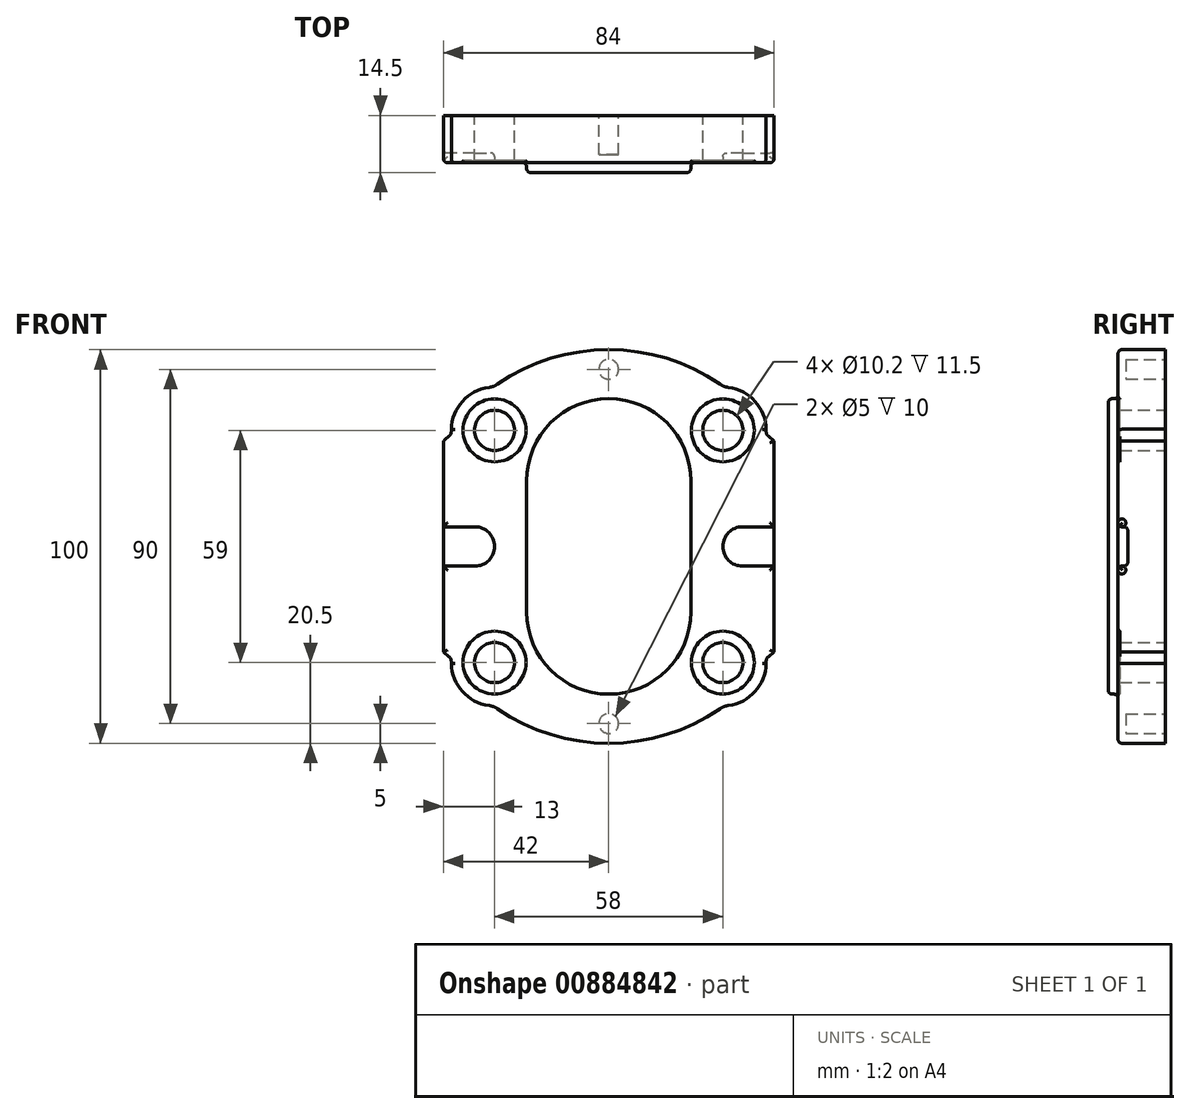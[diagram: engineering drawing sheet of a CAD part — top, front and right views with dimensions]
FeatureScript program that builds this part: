
annotation { "Feature Type Name" : "Feature", "Feature Type Description" : "" }
export const myFeature = defineFeature(function(context is Context, id is Id, definition is map)
    precondition{}
    {
        {
            var Q0;
            Q0=qCreatedBy(makeId("Front.planeOp"),FACE);
            var sketch = newSketch(context, id + "F0", { "sketchPlane" : qUnion([Q0])});
            skArc(sketch, "E0", {"start": v(-28.27, 41.24) * mm, "mid": v(0, 50) * mm, "end": v(28.27, 41.24) * mm});
            skCircle(sketch, "E1", {"center": v(-29, 29.5) * mm, "radius": 5.1 * mm});
            skCircle(sketch, "E2", {"center": v(29, 29.5) * mm, "radius": 5.1 * mm});
            skArc(sketch, "E3", {"start": v(-30.45, 40.4) * mm, "mid": v(-37.18, 36.85) * mm, "end": v(-40, 29.77) * mm});
            skLineSegment(sketch, "E4", {"start": v(-40, 29.77) * mm, "end": v(-40, 29.18) * mm});
            skPoint(sketch, "E5.visualSharp", {"position": v(-29.33, 40.5) * mm});
            skArc(sketch, "E5.filletArc", {"start": v(-30.45, 40.4) * mm, "mid": v(-29.31, 40.7) * mm, "end": v(-28.27, 41.24) * mm});
            skArc(sketch, "E6.MirrorCS", {"start": v(30.45, 40.4) * mm, "mid": v(37.18, 36.85) * mm, "end": v(40, 29.77) * mm});
            skLineSegment(sketch, "E7.MirrorCS", {"start": v(40, 29.77) * mm, "end": v(40, 29.18) * mm});
            skPoint(sketch, "E8.newPointA", {"position": v(29.33, 40.5) * mm});
            skPoint(sketch, "E8.newPointB", {"position": v(30.45, 40.4) * mm});
            skArc(sketch, "E8.filletArc", {"start": v(28.27, 41.24) * mm, "mid": v(29.31, 40.7) * mm, "end": v(30.45, 40.4) * mm});
            skLineSegment(sketch, "E9", {"start": v(-40.55, 28.02) * mm, "end": v(-42, 26.83) * mm});
            skLineSegment(sketch, "E10", {"start": v(-42, 26.83) * mm, "end": v(-42, 0) * mm});
            skPoint(sketch, "E11.visualSharp", {"position": v(-40, 28.47) * mm});
            skArc(sketch, "E11.filletArc", {"start": v(-40.55, 28.02) * mm, "mid": v(-40.14, 28.54) * mm, "end": v(-40, 29.18) * mm});
            skLineSegment(sketch, "E12.MirrorCS", {"start": v(42, 26.83) * mm, "end": v(42, 0) * mm});
            skArc(sketch, "E13.MirrorCS", {"start": v(40.55, 28.02) * mm, "mid": v(40.14, 28.54) * mm, "end": v(40, 29.18) * mm});
            skLineSegment(sketch, "E14.MirrorCS", {"start": v(40.55, 28.02) * mm, "end": v(42, 26.83) * mm});
            skPoint(sketch, "E15.orphan", {"position": v(40, 28.47) * mm});
            skLineSegment(sketch, "E16.MirrorCS", {"start": v(40, -29.77) * mm, "end": v(40, -29.18) * mm});
            skArc(sketch, "E17.MirrorCS", {"start": v(40.55, -28.02) * mm, "mid": v(40.14, -28.54) * mm, "end": v(40, -29.18) * mm});
            skArc(sketch, "E18.MirrorCS", {"start": v(-40.55, -28.02) * mm, "mid": v(-40.14, -28.54) * mm, "end": v(-40, -29.18) * mm});
            skLineSegment(sketch, "E19.MirrorCS", {"start": v(-40, -29.77) * mm, "end": v(-40, -29.18) * mm});
            skArc(sketch, "E20.MirrorCS", {"start": v(28.27, -41.24) * mm, "mid": v(29.31, -40.7) * mm, "end": v(30.45, -40.4) * mm});
            skArc(sketch, "E21.MirrorCS", {"start": v(-30.45, -40.4) * mm, "mid": v(-29.31, -40.7) * mm, "end": v(-28.27, -41.24) * mm});
            skLineSegment(sketch, "E22.MirrorCS", {"start": v(40.55, -28.02) * mm, "end": v(42, -26.83) * mm});
            skLineSegment(sketch, "E23.MirrorCS", {"start": v(-40.55, -28.02) * mm, "end": v(-42, -26.83) * mm});
            skCircle(sketch, "E24.MirrorC", {"center": v(-29, -29.5) * mm, "radius": 5.1 * mm});
            skPoint(sketch, "E25.MirrorP", {"position": v(40, -28.47) * mm});
            skPoint(sketch, "E26.MirrorP", {"position": v(30.45, -40.4) * mm});
            skLineSegment(sketch, "E27.MirrorCS", {"start": v(-42, -26.83) * mm, "end": v(-42, 0) * mm});
            skPoint(sketch, "E28.MirrorP", {"position": v(29.33, -40.5) * mm});
            skCircle(sketch, "E29.MirrorC", {"center": v(29, -29.5) * mm, "radius": 5.1 * mm});
            skArc(sketch, "E30.MirrorCS", {"start": v(30.45, -40.4) * mm, "mid": v(37.18, -36.85) * mm, "end": v(40, -29.77) * mm});
            skArc(sketch, "E31.MirrorCS", {"start": v(-28.27, -41.24) * mm, "mid": v(0, -50) * mm, "end": v(28.27, -41.24) * mm});
            skPoint(sketch, "E32.MirrorP", {"position": v(-29.33, -40.5) * mm});
            skLineSegment(sketch, "E33.MirrorCS", {"start": v(42, -26.83) * mm, "end": v(42, 0) * mm});
            skArc(sketch, "E34.MirrorCS", {"start": v(-30.45, -40.4) * mm, "mid": v(-37.18, -36.85) * mm, "end": v(-40, -29.77) * mm});
            skPoint(sketch, "E35.MirrorP", {"position": v(-40, -28.47) * mm});
            skSolve(sketch);
        }
        {
            var Q0;
            Q0 = qSketchRegion(id + "F0", true);
            extrude(context, id + "F1", {"entities" : qUnion([Q0]), "depth" : 12 * mm, "offsetDistance" : 25 * mm});
        }
        {
            var Q0;
            Q0=makeQuery(id+"F1.opExtrude","CAP_FACE",FACE,{"disambiguationData":[OSD([sQuery(id+"F0.wireOp",EDGE,"E0"),sQuery(id+"F0.wireOp",EDGE,"E1"),sQuery(id+"F0.wireOp",EDGE,"E2"),sQuery(id+"F0.wireOp",EDGE,"E3"),sQuery(id+"F0.wireOp",EDGE,"E4"),sQuery(id+"F0.wireOp",EDGE,"E5.filletArc"),sQuery(id+"F0.wireOp",EDGE,"E6.MirrorCS"),sQuery(id+"F0.wireOp",EDGE,"E8.filletArc"),sQuery(id+"F0.wireOp",EDGE,"E9"),sQuery(id+"F0.wireOp",EDGE,"E10"),sQuery(id+"F0.wireOp",EDGE,"E11.filletArc"),sQuery(id+"F0.wireOp",EDGE,"E12.MirrorCS"),sQuery(id+"F0.wireOp",EDGE,"E7.MirrorCS"),sQuery(id+"F0.wireOp",EDGE,"E13.MirrorCS"),sQuery(id+"F0.wireOp",EDGE,"E14.MirrorCS"),sQuery(id+"F0.wireOp",EDGE,"E17.MirrorCS"),sQuery(id+"F0.wireOp",EDGE,"E16.MirrorCS"),sQuery(id+"F0.wireOp",EDGE,"E18.MirrorCS"),sQuery(id+"F0.wireOp",EDGE,"E19.MirrorCS"),sQuery(id+"F0.wireOp",EDGE,"E20.MirrorCS"),sQuery(id+"F0.wireOp",EDGE,"E21.MirrorCS"),sQuery(id+"F0.wireOp",EDGE,"E22.MirrorCS"),sQuery(id+"F0.wireOp",EDGE,"E23.MirrorCS"),sQuery(id+"F0.wireOp",EDGE,"E24.MirrorC"),sQuery(id+"F0.wireOp",EDGE,"E27.MirrorCS"),sQuery(id+"F0.wireOp",EDGE,"E29.MirrorC"),sQuery(id+"F0.wireOp",EDGE,"E30.MirrorCS"),sQuery(id+"F0.wireOp",EDGE,"E31.MirrorCS"),sQuery(id+"F0.wireOp",EDGE,"E33.MirrorCS"),sQuery(id+"F0.wireOp",EDGE,"E34.MirrorCS")])],"isStart":false});
            var sketch = newSketch(context, id + "F2", { "sketchPlane" : qUnion([Q0])});
            skLineSegment(sketch, "E36", {"start": v(0, 33.36) * mm, "end": v(0, 0) * mm, "construction": true});
            skLineSegment(sketch, "E37", {"start": v(0, 0) * mm, "end": v(54.4, 0) * mm, "construction": true});
            skArc(sketch, "E38", {"start": v(20.85, 16.68) * mm, "mid": v(0, 37.53) * mm, "end": v(-20.85, 16.68) * mm});
            skArc(sketch, "E39.MirrorC", {"start": v(20.85, -16.68) * mm, "mid": v(0, -37.53) * mm, "end": v(-20.85, -16.68) * mm});
            skLineSegment(sketch, "E40", {"start": v(-20.85, 16.68) * mm, "end": v(-20.85, -16.68) * mm});
            skLineSegment(sketch, "E41", {"start": v(20.85, 16.68) * mm, "end": v(20.85, -16.68) * mm});
            skSolve(sketch);
        }
        {
            var Q0;
            Q0 = qSketchRegion(id + "F2", true);
            extrude(context, id + "F3", {"entities" : qUnion([Q0]), "operationType" : NewBodyOperationType.ADD, "depth" : 2.5 * mm, "offsetDistance" : 25 * mm});
        }
        {
            var Q0;
            Q0=makeQuery(id+"F1.opExtrude","CAP_FACE",FACE,{"disambiguationData":[OSD([sQuery(id+"F0.wireOp",EDGE,"E0"),sQuery(id+"F0.wireOp",EDGE,"E1"),sQuery(id+"F0.wireOp",EDGE,"E2"),sQuery(id+"F0.wireOp",EDGE,"E3"),sQuery(id+"F0.wireOp",EDGE,"E4"),sQuery(id+"F0.wireOp",EDGE,"E5.filletArc"),sQuery(id+"F0.wireOp",EDGE,"E6.MirrorCS"),sQuery(id+"F0.wireOp",EDGE,"E8.filletArc"),sQuery(id+"F0.wireOp",EDGE,"E9"),sQuery(id+"F0.wireOp",EDGE,"E10"),sQuery(id+"F0.wireOp",EDGE,"E11.filletArc"),sQuery(id+"F0.wireOp",EDGE,"E12.MirrorCS"),sQuery(id+"F0.wireOp",EDGE,"E7.MirrorCS"),sQuery(id+"F0.wireOp",EDGE,"E13.MirrorCS"),sQuery(id+"F0.wireOp",EDGE,"E14.MirrorCS"),sQuery(id+"F0.wireOp",EDGE,"E17.MirrorCS"),sQuery(id+"F0.wireOp",EDGE,"E16.MirrorCS"),sQuery(id+"F0.wireOp",EDGE,"E18.MirrorCS"),sQuery(id+"F0.wireOp",EDGE,"E19.MirrorCS"),sQuery(id+"F0.wireOp",EDGE,"E20.MirrorCS"),sQuery(id+"F0.wireOp",EDGE,"E21.MirrorCS"),sQuery(id+"F0.wireOp",EDGE,"E22.MirrorCS"),sQuery(id+"F0.wireOp",EDGE,"E23.MirrorCS"),sQuery(id+"F0.wireOp",EDGE,"E24.MirrorC"),sQuery(id+"F0.wireOp",EDGE,"E27.MirrorCS"),sQuery(id+"F0.wireOp",EDGE,"E29.MirrorC"),sQuery(id+"F0.wireOp",EDGE,"E30.MirrorCS"),sQuery(id+"F0.wireOp",EDGE,"E31.MirrorCS"),sQuery(id+"F0.wireOp",EDGE,"E33.MirrorCS"),sQuery(id+"F0.wireOp",EDGE,"E34.MirrorCS")])],"isStart":false});
            var sketch = newSketch(context, id + "F4", { "sketchPlane" : qUnion([Q0])});
            skArc(sketch, "E42", {"start": v(-34, -5) * mm, "mid": v(-29, 0) * mm, "end": v(-34, 5) * mm});
            skLineSegment(sketch, "E43.bottom", {"start": v(-34, 5) * mm, "end": v(-47.92, 5) * mm});
            skLineSegment(sketch, "E43.top", {"start": v(-34, -5) * mm, "end": v(-47.92, -5) * mm});
            skLineSegment(sketch, "E43.right", {"start": v(-47.92, 5) * mm, "end": v(-47.92, -5) * mm});
            skLineSegment(sketch, "E44.MirrorCS", {"start": v(34, -5) * mm, "end": v(47.92, -5) * mm});
            skLineSegment(sketch, "E45.MirrorCS", {"start": v(34, 5) * mm, "end": v(47.92, 5) * mm});
            skLineSegment(sketch, "E46.MirrorCS", {"start": v(47.92, 5) * mm, "end": v(47.92, -5) * mm});
            skArc(sketch, "E47.MirrorCS", {"start": v(34, -5) * mm, "mid": v(29, 0) * mm, "end": v(34, 5) * mm});
            skSolve(sketch);
        }
        {
            var Q0;
            Q0 = qSketchRegion(id + "F4", true);
            extrude(context, id + "F5", {"entities" : qUnion([Q0]), "operationType" : NewBodyOperationType.REMOVE, "oppositeDirection" : true, "depth" : 2.5 * mm, "offsetDistance" : 25 * mm});
        }
        {
            var Q0;
            Q0=makeQuery(id+"F1.opExtrude","CAP_FACE",FACE,{"disambiguationData":[OSD([sQuery(id+"F0.wireOp",EDGE,"E0"),sQuery(id+"F0.wireOp",EDGE,"E1"),sQuery(id+"F0.wireOp",EDGE,"E2"),sQuery(id+"F0.wireOp",EDGE,"E3"),sQuery(id+"F0.wireOp",EDGE,"E4"),sQuery(id+"F0.wireOp",EDGE,"E5.filletArc"),sQuery(id+"F0.wireOp",EDGE,"E6.MirrorCS"),sQuery(id+"F0.wireOp",EDGE,"E8.filletArc"),sQuery(id+"F0.wireOp",EDGE,"E9"),sQuery(id+"F0.wireOp",EDGE,"E10"),sQuery(id+"F0.wireOp",EDGE,"E11.filletArc"),sQuery(id+"F0.wireOp",EDGE,"E12.MirrorCS"),sQuery(id+"F0.wireOp",EDGE,"E7.MirrorCS"),sQuery(id+"F0.wireOp",EDGE,"E13.MirrorCS"),sQuery(id+"F0.wireOp",EDGE,"E14.MirrorCS"),sQuery(id+"F0.wireOp",EDGE,"E17.MirrorCS"),sQuery(id+"F0.wireOp",EDGE,"E16.MirrorCS"),sQuery(id+"F0.wireOp",EDGE,"E18.MirrorCS"),sQuery(id+"F0.wireOp",EDGE,"E19.MirrorCS"),sQuery(id+"F0.wireOp",EDGE,"E20.MirrorCS"),sQuery(id+"F0.wireOp",EDGE,"E21.MirrorCS"),sQuery(id+"F0.wireOp",EDGE,"E22.MirrorCS"),sQuery(id+"F0.wireOp",EDGE,"E23.MirrorCS"),sQuery(id+"F0.wireOp",EDGE,"E24.MirrorC"),sQuery(id+"F0.wireOp",EDGE,"E27.MirrorCS"),sQuery(id+"F0.wireOp",EDGE,"E29.MirrorC"),sQuery(id+"F0.wireOp",EDGE,"E30.MirrorCS"),sQuery(id+"F0.wireOp",EDGE,"E31.MirrorCS"),sQuery(id+"F0.wireOp",EDGE,"E33.MirrorCS"),sQuery(id+"F0.wireOp",EDGE,"E34.MirrorCS")])],"isStart":false});
            var sketch = newSketch(context, id + "F6", { "sketchPlane" : qUnion([Q0])});
            skCircle(sketch, "E48", {"center": v(-29, 29.5) * mm, "radius": 8 * mm});
            skCircle(sketch, "E49", {"center": v(29, 29.5) * mm, "radius": 8 * mm});
            skCircle(sketch, "E50", {"center": v(29, -29.5) * mm, "radius": 8 * mm});
            skCircle(sketch, "E51", {"center": v(-29, -29.5) * mm, "radius": 8 * mm});
            skSolve(sketch);
        }
        {
            var Q0;
            Q0 = qSketchRegion(id + "F6", true);
            extrude(context, id + "F7", {"entities" : qUnion([Q0]), "operationType" : NewBodyOperationType.REMOVE, "oppositeDirection" : true, "depth" : .5 * mm, "offsetDistance" : 25 * mm});
        }
        {
            var Q0;
            Q0=makeQuery(id+"F1.opExtrude","CAP_EDGE",EDGE,{"disambiguationData":[OSD([sQuery(id+"F0.wireOp",EDGE,"E0")])],"isStart":false});
            var Q1;
            {var subQ0=sQuery(id+"F0.wireOp",EDGE,"E33.MirrorCS");var subQ1=sQuery(id+"F0.wireOp",EDGE,"E14.MirrorCS");var subQ2=sQuery(id+"F0.wireOp",EDGE,"E12.MirrorCS");Q1=makeQuery(id+"F5.boolean.opBoolean","SPLIT",EDGE,{"disambiguationData":[TD([makeQuery(id+"F1.opExtrude","SWEPT_FACE",FACE,{"disambiguationData":[OSD([subQ1])]})])],"derivedFrom":makeQuery(id+"F1.opExtrude","CAP_EDGE",EDGE,{"disambiguationData":[OSD([subQ2,subQ0])],"isStart":false})});}
            var Q2;
            Q2=makeQuery(id+"F1.opExtrude","CAP_EDGE",EDGE,{"disambiguationData":[OSD([sQuery(id+"F0.wireOp",EDGE,"E6.MirrorCS")])],"isStart":false});
            var Q3;
            {var subQ0=sQuery(id+"F0.wireOp",EDGE,"E27.MirrorCS");var subQ1=sQuery(id+"F0.wireOp",EDGE,"E10");var subQ2=sQuery(id+"F0.wireOp",EDGE,"E9");Q3=makeQuery(id+"F5.boolean.opBoolean","SPLIT",EDGE,{"disambiguationData":[TD([makeQuery(id+"F1.opExtrude","SWEPT_FACE",FACE,{"disambiguationData":[OSD([subQ2])]})])],"derivedFrom":makeQuery(id+"F1.opExtrude","CAP_EDGE",EDGE,{"disambiguationData":[OSD([subQ1,subQ0])],"isStart":false})});}
            var Q4;
            Q4=makeQuery(id+"F1.opExtrude","CAP_EDGE",EDGE,{"disambiguationData":[OSD([sQuery(id+"F0.wireOp",EDGE,"E11.filletArc")])],"isStart":false});
            var Q5;
            Q5=makeQuery(id+"F1.opExtrude","SWEPT_EDGE",EDGE,{"disambiguationData":[OSD([sQuery(id+"F0.wireOp",EDGE,"E9"),sQuery(id+"F0.wireOp",EDGE,"E10")])]});
            var Q6;
            Q6=makeQuery(id+"F1.opExtrude","CAP_FACE",FACE,{"disambiguationData":[OSD([sQuery(id+"F0.wireOp",EDGE,"E0"),sQuery(id+"F0.wireOp",EDGE,"E1"),sQuery(id+"F0.wireOp",EDGE,"E2"),sQuery(id+"F0.wireOp",EDGE,"E3"),sQuery(id+"F0.wireOp",EDGE,"E4"),sQuery(id+"F0.wireOp",EDGE,"E5.filletArc"),sQuery(id+"F0.wireOp",EDGE,"E6.MirrorCS"),sQuery(id+"F0.wireOp",EDGE,"E8.filletArc"),sQuery(id+"F0.wireOp",EDGE,"E9"),sQuery(id+"F0.wireOp",EDGE,"E10"),sQuery(id+"F0.wireOp",EDGE,"E11.filletArc"),sQuery(id+"F0.wireOp",EDGE,"E12.MirrorCS"),sQuery(id+"F0.wireOp",EDGE,"E7.MirrorCS"),sQuery(id+"F0.wireOp",EDGE,"E13.MirrorCS"),sQuery(id+"F0.wireOp",EDGE,"E14.MirrorCS"),sQuery(id+"F0.wireOp",EDGE,"E17.MirrorCS"),sQuery(id+"F0.wireOp",EDGE,"E16.MirrorCS"),sQuery(id+"F0.wireOp",EDGE,"E18.MirrorCS"),sQuery(id+"F0.wireOp",EDGE,"E19.MirrorCS"),sQuery(id+"F0.wireOp",EDGE,"E20.MirrorCS"),sQuery(id+"F0.wireOp",EDGE,"E21.MirrorCS"),sQuery(id+"F0.wireOp",EDGE,"E22.MirrorCS"),sQuery(id+"F0.wireOp",EDGE,"E23.MirrorCS"),sQuery(id+"F0.wireOp",EDGE,"E24.MirrorC"),sQuery(id+"F0.wireOp",EDGE,"E27.MirrorCS"),sQuery(id+"F0.wireOp",EDGE,"E29.MirrorC"),sQuery(id+"F0.wireOp",EDGE,"E30.MirrorCS"),sQuery(id+"F0.wireOp",EDGE,"E31.MirrorCS"),sQuery(id+"F0.wireOp",EDGE,"E33.MirrorCS"),sQuery(id+"F0.wireOp",EDGE,"E34.MirrorCS")])],"isStart":false});
            fillet(context, id + "F8", {"entities" : qUnion([Q0, Q1, Q2, Q3, Q4, Q5, Q6]), "radius" : 1 * mm, "tangentPropagation" : true, "allowEdgeOverflow" : false});
        }
        {
            var Q0;
            Q0=makeQuery(id+"F8.opFillet","BLEND_EDGE",EDGE,{"blendedFrom":[makeQuery(id+"F3.opExtrude","CAP_EDGE",EDGE,{"disambiguationData":[OSD([sQuery(id+"F2.wireOp",EDGE,"E41")])],"isStart":true}),makeQuery(id+"F1.opExtrude","CAP_FACE",FACE,{"disambiguationData":[OSD([sQuery(id+"F0.wireOp",EDGE,"E0"),sQuery(id+"F0.wireOp",EDGE,"E1"),sQuery(id+"F0.wireOp",EDGE,"E2"),sQuery(id+"F0.wireOp",EDGE,"E3"),sQuery(id+"F0.wireOp",EDGE,"E4"),sQuery(id+"F0.wireOp",EDGE,"E5.filletArc"),sQuery(id+"F0.wireOp",EDGE,"E6.MirrorCS"),sQuery(id+"F0.wireOp",EDGE,"E8.filletArc"),sQuery(id+"F0.wireOp",EDGE,"E9"),sQuery(id+"F0.wireOp",EDGE,"E10"),sQuery(id+"F0.wireOp",EDGE,"E11.filletArc"),sQuery(id+"F0.wireOp",EDGE,"E12.MirrorCS"),sQuery(id+"F0.wireOp",EDGE,"E7.MirrorCS"),sQuery(id+"F0.wireOp",EDGE,"E13.MirrorCS"),sQuery(id+"F0.wireOp",EDGE,"E14.MirrorCS"),sQuery(id+"F0.wireOp",EDGE,"E17.MirrorCS"),sQuery(id+"F0.wireOp",EDGE,"E16.MirrorCS"),sQuery(id+"F0.wireOp",EDGE,"E18.MirrorCS"),sQuery(id+"F0.wireOp",EDGE,"E19.MirrorCS"),sQuery(id+"F0.wireOp",EDGE,"E20.MirrorCS"),sQuery(id+"F0.wireOp",EDGE,"E21.MirrorCS"),sQuery(id+"F0.wireOp",EDGE,"E22.MirrorCS"),sQuery(id+"F0.wireOp",EDGE,"E23.MirrorCS"),sQuery(id+"F0.wireOp",EDGE,"E24.MirrorC"),sQuery(id+"F0.wireOp",EDGE,"E27.MirrorCS"),sQuery(id+"F0.wireOp",EDGE,"E29.MirrorC"),sQuery(id+"F0.wireOp",EDGE,"E30.MirrorCS"),sQuery(id+"F0.wireOp",EDGE,"E31.MirrorCS"),sQuery(id+"F0.wireOp",EDGE,"E33.MirrorCS"),sQuery(id+"F0.wireOp",EDGE,"E34.MirrorCS")])],"isStart":false})],"blendedInto":[makeQuery(id+"F1.opExtrude","CAP_FACE",FACE,{"disambiguationData":[OSD([sQuery(id+"F0.wireOp",EDGE,"E0"),sQuery(id+"F0.wireOp",EDGE,"E1"),sQuery(id+"F0.wireOp",EDGE,"E2"),sQuery(id+"F0.wireOp",EDGE,"E3"),sQuery(id+"F0.wireOp",EDGE,"E4"),sQuery(id+"F0.wireOp",EDGE,"E5.filletArc"),sQuery(id+"F0.wireOp",EDGE,"E6.MirrorCS"),sQuery(id+"F0.wireOp",EDGE,"E8.filletArc"),sQuery(id+"F0.wireOp",EDGE,"E9"),sQuery(id+"F0.wireOp",EDGE,"E10"),sQuery(id+"F0.wireOp",EDGE,"E11.filletArc"),sQuery(id+"F0.wireOp",EDGE,"E12.MirrorCS"),sQuery(id+"F0.wireOp",EDGE,"E7.MirrorCS"),sQuery(id+"F0.wireOp",EDGE,"E13.MirrorCS"),sQuery(id+"F0.wireOp",EDGE,"E14.MirrorCS"),sQuery(id+"F0.wireOp",EDGE,"E17.MirrorCS"),sQuery(id+"F0.wireOp",EDGE,"E16.MirrorCS"),sQuery(id+"F0.wireOp",EDGE,"E18.MirrorCS"),sQuery(id+"F0.wireOp",EDGE,"E19.MirrorCS"),sQuery(id+"F0.wireOp",EDGE,"E20.MirrorCS"),sQuery(id+"F0.wireOp",EDGE,"E21.MirrorCS"),sQuery(id+"F0.wireOp",EDGE,"E22.MirrorCS"),sQuery(id+"F0.wireOp",EDGE,"E23.MirrorCS"),sQuery(id+"F0.wireOp",EDGE,"E24.MirrorC"),sQuery(id+"F0.wireOp",EDGE,"E27.MirrorCS"),sQuery(id+"F0.wireOp",EDGE,"E29.MirrorC"),sQuery(id+"F0.wireOp",EDGE,"E30.MirrorCS"),sQuery(id+"F0.wireOp",EDGE,"E31.MirrorCS"),sQuery(id+"F0.wireOp",EDGE,"E33.MirrorCS"),sQuery(id+"F0.wireOp",EDGE,"E34.MirrorCS")])],"isStart":false})]});
            var Q1;
            Q1=makeQuery(id+"F8.opFillet","BLEND_EDGE",EDGE,{"blendedFrom":[makeQuery(id+"F3.opExtrude","CAP_EDGE",EDGE,{"disambiguationData":[OSD([sQuery(id+"F2.wireOp",EDGE,"E38")])],"isStart":true}),makeQuery(id+"F1.opExtrude","CAP_FACE",FACE,{"disambiguationData":[OSD([sQuery(id+"F0.wireOp",EDGE,"E0"),sQuery(id+"F0.wireOp",EDGE,"E1"),sQuery(id+"F0.wireOp",EDGE,"E2"),sQuery(id+"F0.wireOp",EDGE,"E3"),sQuery(id+"F0.wireOp",EDGE,"E4"),sQuery(id+"F0.wireOp",EDGE,"E5.filletArc"),sQuery(id+"F0.wireOp",EDGE,"E6.MirrorCS"),sQuery(id+"F0.wireOp",EDGE,"E8.filletArc"),sQuery(id+"F0.wireOp",EDGE,"E9"),sQuery(id+"F0.wireOp",EDGE,"E10"),sQuery(id+"F0.wireOp",EDGE,"E11.filletArc"),sQuery(id+"F0.wireOp",EDGE,"E12.MirrorCS"),sQuery(id+"F0.wireOp",EDGE,"E7.MirrorCS"),sQuery(id+"F0.wireOp",EDGE,"E13.MirrorCS"),sQuery(id+"F0.wireOp",EDGE,"E14.MirrorCS"),sQuery(id+"F0.wireOp",EDGE,"E17.MirrorCS"),sQuery(id+"F0.wireOp",EDGE,"E16.MirrorCS"),sQuery(id+"F0.wireOp",EDGE,"E18.MirrorCS"),sQuery(id+"F0.wireOp",EDGE,"E19.MirrorCS"),sQuery(id+"F0.wireOp",EDGE,"E20.MirrorCS"),sQuery(id+"F0.wireOp",EDGE,"E21.MirrorCS"),sQuery(id+"F0.wireOp",EDGE,"E22.MirrorCS"),sQuery(id+"F0.wireOp",EDGE,"E23.MirrorCS"),sQuery(id+"F0.wireOp",EDGE,"E24.MirrorC"),sQuery(id+"F0.wireOp",EDGE,"E27.MirrorCS"),sQuery(id+"F0.wireOp",EDGE,"E29.MirrorC"),sQuery(id+"F0.wireOp",EDGE,"E30.MirrorCS"),sQuery(id+"F0.wireOp",EDGE,"E31.MirrorCS"),sQuery(id+"F0.wireOp",EDGE,"E33.MirrorCS"),sQuery(id+"F0.wireOp",EDGE,"E34.MirrorCS")])],"isStart":false})],"blendedInto":[makeQuery(id+"F1.opExtrude","CAP_FACE",FACE,{"disambiguationData":[OSD([sQuery(id+"F0.wireOp",EDGE,"E0"),sQuery(id+"F0.wireOp",EDGE,"E1"),sQuery(id+"F0.wireOp",EDGE,"E2"),sQuery(id+"F0.wireOp",EDGE,"E3"),sQuery(id+"F0.wireOp",EDGE,"E4"),sQuery(id+"F0.wireOp",EDGE,"E5.filletArc"),sQuery(id+"F0.wireOp",EDGE,"E6.MirrorCS"),sQuery(id+"F0.wireOp",EDGE,"E8.filletArc"),sQuery(id+"F0.wireOp",EDGE,"E9"),sQuery(id+"F0.wireOp",EDGE,"E10"),sQuery(id+"F0.wireOp",EDGE,"E11.filletArc"),sQuery(id+"F0.wireOp",EDGE,"E12.MirrorCS"),sQuery(id+"F0.wireOp",EDGE,"E7.MirrorCS"),sQuery(id+"F0.wireOp",EDGE,"E13.MirrorCS"),sQuery(id+"F0.wireOp",EDGE,"E14.MirrorCS"),sQuery(id+"F0.wireOp",EDGE,"E17.MirrorCS"),sQuery(id+"F0.wireOp",EDGE,"E16.MirrorCS"),sQuery(id+"F0.wireOp",EDGE,"E18.MirrorCS"),sQuery(id+"F0.wireOp",EDGE,"E19.MirrorCS"),sQuery(id+"F0.wireOp",EDGE,"E20.MirrorCS"),sQuery(id+"F0.wireOp",EDGE,"E21.MirrorCS"),sQuery(id+"F0.wireOp",EDGE,"E22.MirrorCS"),sQuery(id+"F0.wireOp",EDGE,"E23.MirrorCS"),sQuery(id+"F0.wireOp",EDGE,"E24.MirrorC"),sQuery(id+"F0.wireOp",EDGE,"E27.MirrorCS"),sQuery(id+"F0.wireOp",EDGE,"E29.MirrorC"),sQuery(id+"F0.wireOp",EDGE,"E30.MirrorCS"),sQuery(id+"F0.wireOp",EDGE,"E31.MirrorCS"),sQuery(id+"F0.wireOp",EDGE,"E33.MirrorCS"),sQuery(id+"F0.wireOp",EDGE,"E34.MirrorCS")])],"isStart":false})]});
            var Q2;
            Q2=makeQuery(id+"F8.opFillet","BLEND_EDGE",EDGE,{"blendedFrom":[makeQuery(id+"F3.opExtrude","CAP_EDGE",EDGE,{"disambiguationData":[OSD([sQuery(id+"F2.wireOp",EDGE,"E39.MirrorC")])],"isStart":true}),makeQuery(id+"F1.opExtrude","CAP_FACE",FACE,{"disambiguationData":[OSD([sQuery(id+"F0.wireOp",EDGE,"E0"),sQuery(id+"F0.wireOp",EDGE,"E1"),sQuery(id+"F0.wireOp",EDGE,"E2"),sQuery(id+"F0.wireOp",EDGE,"E3"),sQuery(id+"F0.wireOp",EDGE,"E4"),sQuery(id+"F0.wireOp",EDGE,"E5.filletArc"),sQuery(id+"F0.wireOp",EDGE,"E6.MirrorCS"),sQuery(id+"F0.wireOp",EDGE,"E8.filletArc"),sQuery(id+"F0.wireOp",EDGE,"E9"),sQuery(id+"F0.wireOp",EDGE,"E10"),sQuery(id+"F0.wireOp",EDGE,"E11.filletArc"),sQuery(id+"F0.wireOp",EDGE,"E12.MirrorCS"),sQuery(id+"F0.wireOp",EDGE,"E7.MirrorCS"),sQuery(id+"F0.wireOp",EDGE,"E13.MirrorCS"),sQuery(id+"F0.wireOp",EDGE,"E14.MirrorCS"),sQuery(id+"F0.wireOp",EDGE,"E17.MirrorCS"),sQuery(id+"F0.wireOp",EDGE,"E16.MirrorCS"),sQuery(id+"F0.wireOp",EDGE,"E18.MirrorCS"),sQuery(id+"F0.wireOp",EDGE,"E19.MirrorCS"),sQuery(id+"F0.wireOp",EDGE,"E20.MirrorCS"),sQuery(id+"F0.wireOp",EDGE,"E21.MirrorCS"),sQuery(id+"F0.wireOp",EDGE,"E22.MirrorCS"),sQuery(id+"F0.wireOp",EDGE,"E23.MirrorCS"),sQuery(id+"F0.wireOp",EDGE,"E24.MirrorC"),sQuery(id+"F0.wireOp",EDGE,"E27.MirrorCS"),sQuery(id+"F0.wireOp",EDGE,"E29.MirrorC"),sQuery(id+"F0.wireOp",EDGE,"E30.MirrorCS"),sQuery(id+"F0.wireOp",EDGE,"E31.MirrorCS"),sQuery(id+"F0.wireOp",EDGE,"E33.MirrorCS"),sQuery(id+"F0.wireOp",EDGE,"E34.MirrorCS")])],"isStart":false})],"blendedInto":[makeQuery(id+"F1.opExtrude","CAP_FACE",FACE,{"disambiguationData":[OSD([sQuery(id+"F0.wireOp",EDGE,"E0"),sQuery(id+"F0.wireOp",EDGE,"E1"),sQuery(id+"F0.wireOp",EDGE,"E2"),sQuery(id+"F0.wireOp",EDGE,"E3"),sQuery(id+"F0.wireOp",EDGE,"E4"),sQuery(id+"F0.wireOp",EDGE,"E5.filletArc"),sQuery(id+"F0.wireOp",EDGE,"E6.MirrorCS"),sQuery(id+"F0.wireOp",EDGE,"E8.filletArc"),sQuery(id+"F0.wireOp",EDGE,"E9"),sQuery(id+"F0.wireOp",EDGE,"E10"),sQuery(id+"F0.wireOp",EDGE,"E11.filletArc"),sQuery(id+"F0.wireOp",EDGE,"E12.MirrorCS"),sQuery(id+"F0.wireOp",EDGE,"E7.MirrorCS"),sQuery(id+"F0.wireOp",EDGE,"E13.MirrorCS"),sQuery(id+"F0.wireOp",EDGE,"E14.MirrorCS"),sQuery(id+"F0.wireOp",EDGE,"E17.MirrorCS"),sQuery(id+"F0.wireOp",EDGE,"E16.MirrorCS"),sQuery(id+"F0.wireOp",EDGE,"E18.MirrorCS"),sQuery(id+"F0.wireOp",EDGE,"E19.MirrorCS"),sQuery(id+"F0.wireOp",EDGE,"E20.MirrorCS"),sQuery(id+"F0.wireOp",EDGE,"E21.MirrorCS"),sQuery(id+"F0.wireOp",EDGE,"E22.MirrorCS"),sQuery(id+"F0.wireOp",EDGE,"E23.MirrorCS"),sQuery(id+"F0.wireOp",EDGE,"E24.MirrorC"),sQuery(id+"F0.wireOp",EDGE,"E27.MirrorCS"),sQuery(id+"F0.wireOp",EDGE,"E29.MirrorC"),sQuery(id+"F0.wireOp",EDGE,"E30.MirrorCS"),sQuery(id+"F0.wireOp",EDGE,"E31.MirrorCS"),sQuery(id+"F0.wireOp",EDGE,"E33.MirrorCS"),sQuery(id+"F0.wireOp",EDGE,"E34.MirrorCS")])],"isStart":false})]});
            var Q3;
            Q3=makeQuery(id+"F3.opExtrude","CAP_EDGE",EDGE,{"disambiguationData":[OSD([sQuery(id+"F2.wireOp",EDGE,"E39.MirrorC")])],"isStart":false});
            var Q4;
            Q4=makeQuery(id+"F3.opExtrude","CAP_EDGE",EDGE,{"disambiguationData":[OSD([sQuery(id+"F2.wireOp",EDGE,"E41")])],"isStart":false});
            var Q5;
            Q5=makeQuery(id+"F3.opExtrude","CAP_EDGE",EDGE,{"disambiguationData":[OSD([sQuery(id+"F2.wireOp",EDGE,"E38")])],"isStart":false});
            var Q6;
            Q6=makeQuery(id+"F3.opExtrude","CAP_EDGE",EDGE,{"disambiguationData":[OSD([sQuery(id+"F2.wireOp",EDGE,"E40")])],"isStart":false});
            var Q7;
            Q7=makeQuery(id+"F8.opFillet","BLEND_EDGE",EDGE,{"blendedFrom":[makeQuery(id+"F3.opExtrude","CAP_EDGE",EDGE,{"disambiguationData":[OSD([sQuery(id+"F2.wireOp",EDGE,"E40")])],"isStart":true}),makeQuery(id+"F1.opExtrude","CAP_FACE",FACE,{"disambiguationData":[OSD([sQuery(id+"F0.wireOp",EDGE,"E0"),sQuery(id+"F0.wireOp",EDGE,"E1"),sQuery(id+"F0.wireOp",EDGE,"E2"),sQuery(id+"F0.wireOp",EDGE,"E3"),sQuery(id+"F0.wireOp",EDGE,"E4"),sQuery(id+"F0.wireOp",EDGE,"E5.filletArc"),sQuery(id+"F0.wireOp",EDGE,"E6.MirrorCS"),sQuery(id+"F0.wireOp",EDGE,"E8.filletArc"),sQuery(id+"F0.wireOp",EDGE,"E9"),sQuery(id+"F0.wireOp",EDGE,"E10"),sQuery(id+"F0.wireOp",EDGE,"E11.filletArc"),sQuery(id+"F0.wireOp",EDGE,"E12.MirrorCS"),sQuery(id+"F0.wireOp",EDGE,"E7.MirrorCS"),sQuery(id+"F0.wireOp",EDGE,"E13.MirrorCS"),sQuery(id+"F0.wireOp",EDGE,"E14.MirrorCS"),sQuery(id+"F0.wireOp",EDGE,"E17.MirrorCS"),sQuery(id+"F0.wireOp",EDGE,"E16.MirrorCS"),sQuery(id+"F0.wireOp",EDGE,"E18.MirrorCS"),sQuery(id+"F0.wireOp",EDGE,"E19.MirrorCS"),sQuery(id+"F0.wireOp",EDGE,"E20.MirrorCS"),sQuery(id+"F0.wireOp",EDGE,"E21.MirrorCS"),sQuery(id+"F0.wireOp",EDGE,"E22.MirrorCS"),sQuery(id+"F0.wireOp",EDGE,"E23.MirrorCS"),sQuery(id+"F0.wireOp",EDGE,"E24.MirrorC"),sQuery(id+"F0.wireOp",EDGE,"E27.MirrorCS"),sQuery(id+"F0.wireOp",EDGE,"E29.MirrorC"),sQuery(id+"F0.wireOp",EDGE,"E30.MirrorCS"),sQuery(id+"F0.wireOp",EDGE,"E31.MirrorCS"),sQuery(id+"F0.wireOp",EDGE,"E33.MirrorCS"),sQuery(id+"F0.wireOp",EDGE,"E34.MirrorCS")])],"isStart":false})],"blendedInto":[makeQuery(id+"F1.opExtrude","CAP_FACE",FACE,{"disambiguationData":[OSD([sQuery(id+"F0.wireOp",EDGE,"E0"),sQuery(id+"F0.wireOp",EDGE,"E1"),sQuery(id+"F0.wireOp",EDGE,"E2"),sQuery(id+"F0.wireOp",EDGE,"E3"),sQuery(id+"F0.wireOp",EDGE,"E4"),sQuery(id+"F0.wireOp",EDGE,"E5.filletArc"),sQuery(id+"F0.wireOp",EDGE,"E6.MirrorCS"),sQuery(id+"F0.wireOp",EDGE,"E8.filletArc"),sQuery(id+"F0.wireOp",EDGE,"E9"),sQuery(id+"F0.wireOp",EDGE,"E10"),sQuery(id+"F0.wireOp",EDGE,"E11.filletArc"),sQuery(id+"F0.wireOp",EDGE,"E12.MirrorCS"),sQuery(id+"F0.wireOp",EDGE,"E7.MirrorCS"),sQuery(id+"F0.wireOp",EDGE,"E13.MirrorCS"),sQuery(id+"F0.wireOp",EDGE,"E14.MirrorCS"),sQuery(id+"F0.wireOp",EDGE,"E17.MirrorCS"),sQuery(id+"F0.wireOp",EDGE,"E16.MirrorCS"),sQuery(id+"F0.wireOp",EDGE,"E18.MirrorCS"),sQuery(id+"F0.wireOp",EDGE,"E19.MirrorCS"),sQuery(id+"F0.wireOp",EDGE,"E20.MirrorCS"),sQuery(id+"F0.wireOp",EDGE,"E21.MirrorCS"),sQuery(id+"F0.wireOp",EDGE,"E22.MirrorCS"),sQuery(id+"F0.wireOp",EDGE,"E23.MirrorCS"),sQuery(id+"F0.wireOp",EDGE,"E24.MirrorC"),sQuery(id+"F0.wireOp",EDGE,"E27.MirrorCS"),sQuery(id+"F0.wireOp",EDGE,"E29.MirrorC"),sQuery(id+"F0.wireOp",EDGE,"E30.MirrorCS"),sQuery(id+"F0.wireOp",EDGE,"E31.MirrorCS"),sQuery(id+"F0.wireOp",EDGE,"E33.MirrorCS"),sQuery(id+"F0.wireOp",EDGE,"E34.MirrorCS")])],"isStart":false})]});
            fillet(context, id + "F9", {"entities" : qUnion([Q0, Q1, Q2, Q3, Q4, Q5, Q6, Q7]), "radius" : 1 * mm, "tangentPropagation" : true, "allowEdgeOverflow" : false});
        }
        {
            var Q0;
            Q0=makeQuery(id+"F5.boolean.opBoolean","COPY",FACE,{"derivedFrom":makeQuery(id+"F5.opExtrude","CAP_FACE",FACE,{"disambiguationData":[OSD([sQuery(id+"F4.wireOp",EDGE,"E44.MirrorCS"),sQuery(id+"F4.wireOp",EDGE,"E45.MirrorCS"),sQuery(id+"F4.wireOp",EDGE,"E46.MirrorCS"),sQuery(id+"F4.wireOp",EDGE,"E47.MirrorCS")])],"isStart":false})});
            var Q1;
            Q1=makeQuery(id+"F5.boolean.opBoolean","COPY",FACE,{"derivedFrom":makeQuery(id+"F5.opExtrude","CAP_FACE",FACE,{"disambiguationData":[OSD([sQuery(id+"F4.wireOp",EDGE,"E42"),sQuery(id+"F4.wireOp",EDGE,"E43.bottom"),sQuery(id+"F4.wireOp",EDGE,"E43.top"),sQuery(id+"F4.wireOp",EDGE,"E43.right")])],"isStart":false})});
            fillet(context, id + "F10", {"entities" : qUnion([Q0, Q1]), "radius" : 1 * mm, "tangentPropagation" : true, "allowEdgeOverflow" : false});
        }
        {
            var Q0;
            Q0=makeQuery(id+"F1.opExtrude","CAP_FACE",FACE,{"disambiguationData":[OSD([sQuery(id+"F0.wireOp",EDGE,"E0"),sQuery(id+"F0.wireOp",EDGE,"E1"),sQuery(id+"F0.wireOp",EDGE,"E2"),sQuery(id+"F0.wireOp",EDGE,"E3"),sQuery(id+"F0.wireOp",EDGE,"E4"),sQuery(id+"F0.wireOp",EDGE,"E5.filletArc"),sQuery(id+"F0.wireOp",EDGE,"E6.MirrorCS"),sQuery(id+"F0.wireOp",EDGE,"E8.filletArc"),sQuery(id+"F0.wireOp",EDGE,"E9"),sQuery(id+"F0.wireOp",EDGE,"E10"),sQuery(id+"F0.wireOp",EDGE,"E11.filletArc"),sQuery(id+"F0.wireOp",EDGE,"E12.MirrorCS"),sQuery(id+"F0.wireOp",EDGE,"E7.MirrorCS"),sQuery(id+"F0.wireOp",EDGE,"E13.MirrorCS"),sQuery(id+"F0.wireOp",EDGE,"E14.MirrorCS"),sQuery(id+"F0.wireOp",EDGE,"E17.MirrorCS"),sQuery(id+"F0.wireOp",EDGE,"E16.MirrorCS"),sQuery(id+"F0.wireOp",EDGE,"E18.MirrorCS"),sQuery(id+"F0.wireOp",EDGE,"E19.MirrorCS"),sQuery(id+"F0.wireOp",EDGE,"E20.MirrorCS"),sQuery(id+"F0.wireOp",EDGE,"E21.MirrorCS"),sQuery(id+"F0.wireOp",EDGE,"E22.MirrorCS"),sQuery(id+"F0.wireOp",EDGE,"E23.MirrorCS"),sQuery(id+"F0.wireOp",EDGE,"E24.MirrorC"),sQuery(id+"F0.wireOp",EDGE,"E27.MirrorCS"),sQuery(id+"F0.wireOp",EDGE,"E29.MirrorC"),sQuery(id+"F0.wireOp",EDGE,"E30.MirrorCS"),sQuery(id+"F0.wireOp",EDGE,"E31.MirrorCS"),sQuery(id+"F0.wireOp",EDGE,"E33.MirrorCS"),sQuery(id+"F0.wireOp",EDGE,"E34.MirrorCS")])],"isStart":true});
            var sketch = newSketch(context, id + "F11", { "sketchPlane" : qUnion([Q0])});
            skCircle(sketch, "E52", {"center": v(0, 45) * mm, "radius": 2.5 * mm});
            skCircle(sketch, "E53", {"center": v(0, -45) * mm, "radius": 2.5 * mm});
            skSolve(sketch);
        }
        {
            var Q0;
            Q0 = qSketchRegion(id + "F11", true);
            extrude(context, id + "F12", {"entities" : qUnion([Q0]), "operationType" : NewBodyOperationType.REMOVE, "oppositeDirection" : true, "depth" : 10 * mm, "offsetDistance" : 25 * mm});
        }
    });
